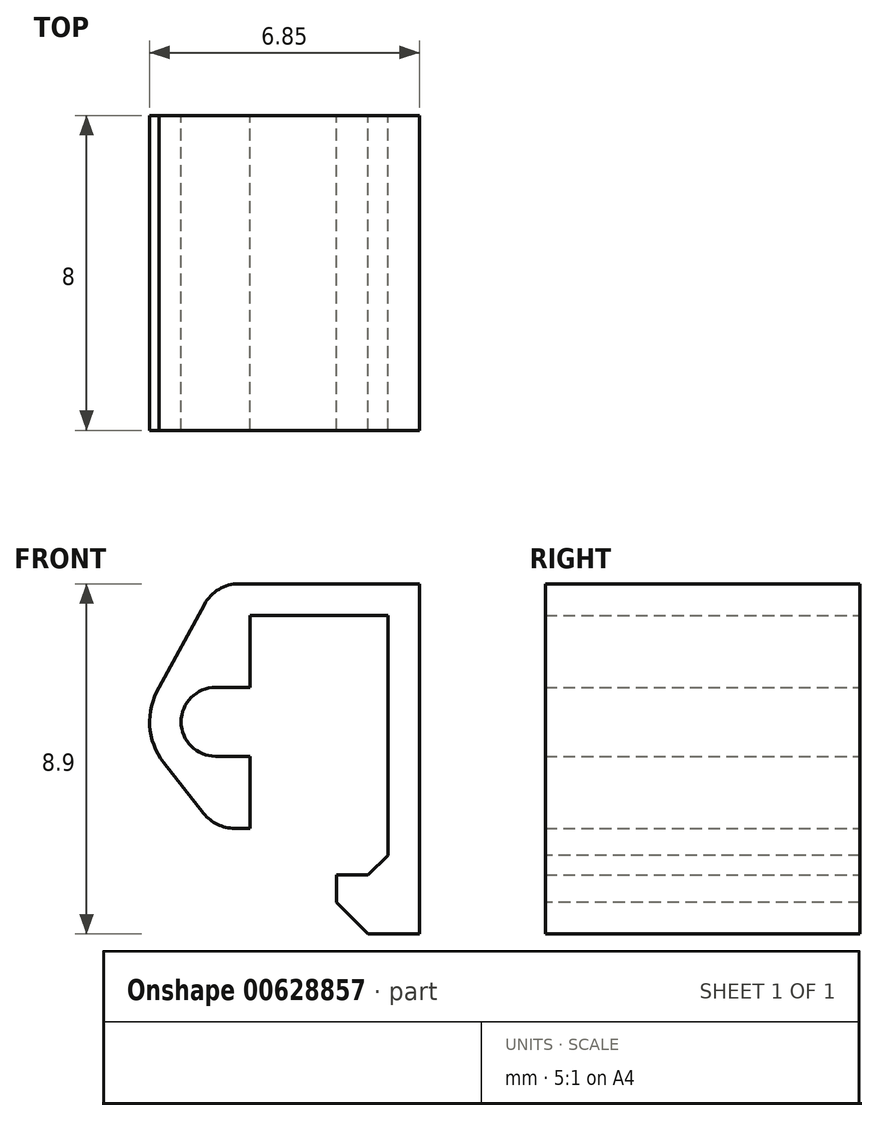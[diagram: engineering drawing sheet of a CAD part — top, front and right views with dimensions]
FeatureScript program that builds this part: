
annotation { "Feature Type Name" : "Feature", "Feature Type Description" : "" }
export const myFeature = defineFeature(function(context is Context, id is Id, definition is map)
    precondition{}
    {
        {
            var Q0;
            Q0=qCreatedBy(makeId("Front.planeOp"),FACE);
            var sketch = newSketch(context, id + "F0", { "sketchPlane" : qUnion([Q0])});
            skLineSegment(sketch, "E0", {"start": v(0, 0) * mm, "end": v(0, 6.6) * mm});
            skLineSegment(sketch, "E1", {"start": v(0, 6.6) * mm, "end": v(-3.5, 6.6) * mm});
            skLineSegment(sketch, "E2", {"start": v(-3.5, 6.6) * mm, "end": v(-3.5, 1.19) * mm, "construction": true});
            skPoint(sketch, "E3", {"position": v(-3.5, 3.9) * mm});
            skPoint(sketch, "E4", {"position": v(-4.38, 3.9) * mm});
            skCircle(sketch, "E5", {"center": v(-4.38, 3.9) * mm, "radius": 0.87 * mm, "construction": true});
            skLineSegment(sketch, "E6", {"start": v(-4.38, 4.77) * mm, "end": v(-3.5, 4.77) * mm});
            skLineSegment(sketch, "E7", {"start": v(-4.38, 3.02) * mm, "end": v(-3.5, 3.02) * mm});
            skLineSegment(sketch, "E8", {"start": v(-3.5, 3.02) * mm, "end": v(-3.5, 1.19) * mm});
            skLineSegment(sketch, "E9", {"start": v(0, 0) * mm, "end": v(-1.3, 0) * mm});
            skCircle(sketch, "E10", {"center": v(-4.38, 3.9) * mm, "radius": 1.68 * mm, "construction": true});
            skLineSegment(sketch, "E11.0", {"start": v(0.8, 7.4) * mm, "end": v(-3.5, 7.4) * mm});
            skLineSegment(sketch, "E11.1", {"start": v(0.8, 0) * mm, "end": v(0.8, 7.4) * mm});
            skLineSegment(sketch, "E12", {"start": v(-3.5, 7.4) * mm, "end": v(-4.38, 7.4) * mm});
            skLineSegment(sketch, "E13", {"start": v(-3.5, 1.19) * mm, "end": v(-4.38, 1.19) * mm});
            skLineSegment(sketch, "E14", {"start": v(-4.38, 7.4) * mm, "end": v(-5.8, 4.77) * mm});
            skLineSegment(sketch, "E15", {"start": v(-4.38, 1.19) * mm, "end": v(-5.7, 2.86) * mm});
            skLineSegment(sketch, "E16", {"start": v(0.8, 0) * mm, "end": v(0.8, -1.5) * mm});
            skLineSegment(sketch, "E17", {"start": v(-1.3, 0) * mm, "end": v(-1.3, -1.5) * mm});
            skLineSegment(sketch, "E18", {"start": v(0.8, -1.5) * mm, "end": v(-1.3, -1.5) * mm});
            skLineSegment(sketch, "E19", {"start": v(-3.5, 4.77) * mm, "end": v(-3.5, 6.6) * mm});
            skArc(sketch, "E20", {"start": v(-5.8, 4.77) * mm, "mid": v(-6.05, 3.8) * mm, "end": v(-5.7, 2.86) * mm});
            skArc(sketch, "E21", {"start": v(-4.38, 4.77) * mm, "mid": v(-5.25, 3.9) * mm, "end": v(-4.38, 3.02) * mm});
            skSolve(sketch);
        }
        {
            var Q0;
            Q0=makeQuery(id+"F0.imprint","IMPRINT",FACE,{"disambiguationData":[TD([[makeQuery(id+"F0.imprint","IMPRINT",EDGE,{"derivedFrom":sQuery(id+"F0.wireOp",EDGE,"E0")}),-1.0]])]});
            extrude(context, id + "F1", {"entities" : qUnion([Q0]), "depth" : 8 * mm, "offsetDistance" : 25 * mm});
        }
        {
            var Q0;
            Q0=makeQuery(id+"F1.opExtrude","SWEPT_EDGE",EDGE,{"disambiguationData":[OSD([sQuery(id+"F0.wireOp",EDGE,"E0"),sQuery(id+"F0.wireOp",EDGE,"E9")])]});
            chamfer(context, id + "F2", {"entities" : qUnion([Q0]), "width" : .5 * mm, "tangentPropagation" : true});
        }
        {
            var Q0;
            Q0=makeQuery(id+"F1.opExtrude","SWEPT_EDGE",EDGE,{"disambiguationData":[OSD([sQuery(id+"F0.wireOp",EDGE,"E17"),sQuery(id+"F0.wireOp",EDGE,"E18")])]});
            chamfer(context, id + "F3", {"entities" : qUnion([Q0]), "width" : .8 * mm, "tangentPropagation" : true});
        }
        {
            var Q0;
            Q0=makeQuery(id+"F1.opExtrude","SWEPT_EDGE",EDGE,{"disambiguationData":[OSD([sQuery(id+"F0.wireOp",EDGE,"E13"),sQuery(id+"F0.wireOp",EDGE,"E15")])]});
            var Q1;
            Q1=makeQuery(id+"F1.opExtrude","SWEPT_EDGE",EDGE,{"disambiguationData":[OSD([sQuery(id+"F0.wireOp",EDGE,"E12"),sQuery(id+"F0.wireOp",EDGE,"E14")])]});
            fillet(context, id + "F4", {"entities" : qUnion([Q0, Q1]), "radius" : 1 * mm, "tangentPropagation" : true, "allowEdgeOverflow" : false});
        }
    });
